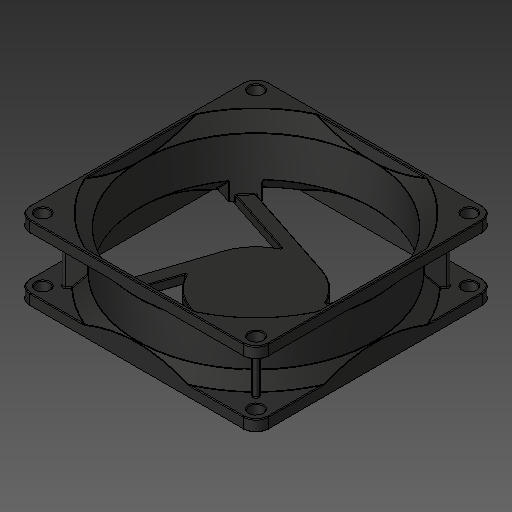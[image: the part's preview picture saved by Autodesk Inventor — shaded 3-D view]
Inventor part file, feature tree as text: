
AUTODESK INVENTOR PART (.ipt)
format: ipt  version: 2018.2 (Build 222227000, 227)  size: 1,625,600 bytes
history: native  units: mm
features: other x1, fillet x1
ambient origin geometry x8: Origin, YZ Plane, XZ Plane, XY Plane, X Axis, Y Axis, Z Axis, Center Point
bodies: Body1 (feature_tree)
feature tree (2):
  other  "ソリッド1"
  fillet  "Fillet1"  [1 undecoded]
note: 1 required parameter value undecoded (feature->parameter linkage not recoverable at this tier; creation-order binding heuristic only, values carry confidence <= 0.55)
